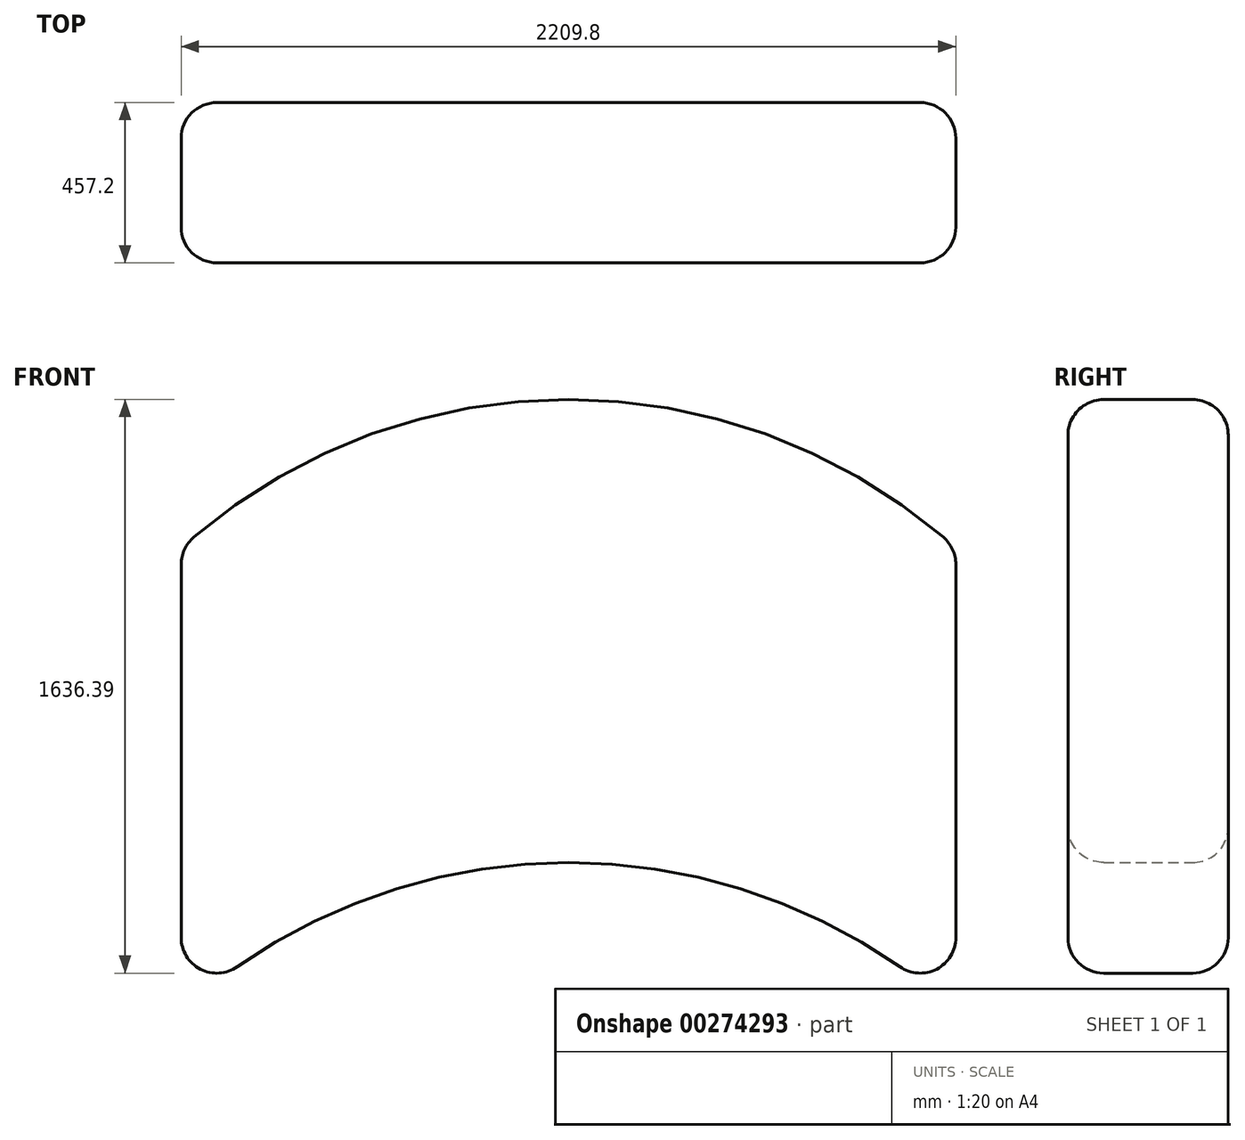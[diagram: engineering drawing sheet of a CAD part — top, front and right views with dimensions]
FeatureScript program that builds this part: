
annotation { "Feature Type Name" : "Feature", "Feature Type Description" : "" }
export const myFeature = defineFeature(function(context is Context, id is Id, definition is map)
    precondition{}
    {
        {
            var Q0;
            Q0=qCreatedBy(makeId("Front.planeOp"),FACE);
            var sketch = newSketch(context, id + "F0", { "sketchPlane" : qUnion([Q0])});
            skLineSegment(sketch, "E0", {"start": v(0, 0) * mm, "end": v(1104.9, 0) * mm});
            skLineSegment(sketch, "E1", {"start": v(0, 0) * mm, "end": v(-1104.9, 0) * mm});
            skLineSegment(sketch, "E2", {"start": v(-1104.9, 0) * mm, "end": v(-1104.9, 1320.8) * mm});
            skLineSegment(sketch, "E3", {"start": v(1104.9, 0) * mm, "end": v(1104.9, 1320.8) * mm});
            skArc(sketch, "E4", {"start": v(1104.9, 1320.8) * mm, "mid": v(0, 1745.02) * mm, "end": v(-1104.9, 1320.8) * mm});
            skArc(sketch, "E5", {"start": v(1104.9, 0) * mm, "mid": v(0, 424.22) * mm, "end": v(-1104.9, 0) * mm});
            skSolve(sketch);
        }
        {
            var Q0;
            Q0=makeQuery(id+"F0.imprint","IMPRINT",FACE,{"disambiguationData":[TD([[makeQuery(id+"F0.imprint","IMPRINT",EDGE,{"derivedFrom":sQuery(id+"F0.wireOp",EDGE,"E2")}),-1.0]])]});
            extrude(context, id + "F1", {"entities" : qUnion([Q0]), "depth" : 457.2 * mm});
        }
        {
            var Q0;
            Q0=makeQuery(id+"F1.opExtrude","CAP_FACE",FACE,{"disambiguationData":[OSD([sQuery(id+"F0.wireOp",EDGE,"E2"),sQuery(id+"F0.wireOp",EDGE,"E3"),sQuery(id+"F0.wireOp",EDGE,"E4"),sQuery(id+"F0.wireOp",EDGE,"E5")])],"isStart":true});
            var Q1;
            Q1=makeQuery(id+"F1.opExtrude","SWEPT_FACE",FACE,{"disambiguationData":[OSD([sQuery(id+"F0.wireOp",EDGE,"E2")])]});
            var Q2;
            Q2=makeQuery(id+"F1.opExtrude","CAP_EDGE",EDGE,{"disambiguationData":[OSD([sQuery(id+"F0.wireOp",EDGE,"E5")])],"isStart":false});
            var Q3;
            Q3=makeQuery(id+"F1.opExtrude","SWEPT_FACE",FACE,{"disambiguationData":[OSD([sQuery(id+"F0.wireOp",EDGE,"E3")])]});
            var Q4;
            Q4=makeQuery(id+"F1.opExtrude","CAP_FACE",FACE,{"disambiguationData":[OSD([sQuery(id+"F0.wireOp",EDGE,"E2"),sQuery(id+"F0.wireOp",EDGE,"E3"),sQuery(id+"F0.wireOp",EDGE,"E4"),sQuery(id+"F0.wireOp",EDGE,"E5")])],"isStart":false});
            var Q5;
            Q5=makeQuery(id+"F1.opExtrude","SWEPT_FACE",FACE,{"disambiguationData":[OSD([sQuery(id+"F0.wireOp",EDGE,"E4")])]});
            fillet(context, id + "F2", {"entities" : qUnion([Q0, Q1, Q2, Q3, Q4, Q5]), "radius" : 101.6 * mm, "tangentPropagation" : true, "allowEdgeOverflow" : false});
        }
    });
